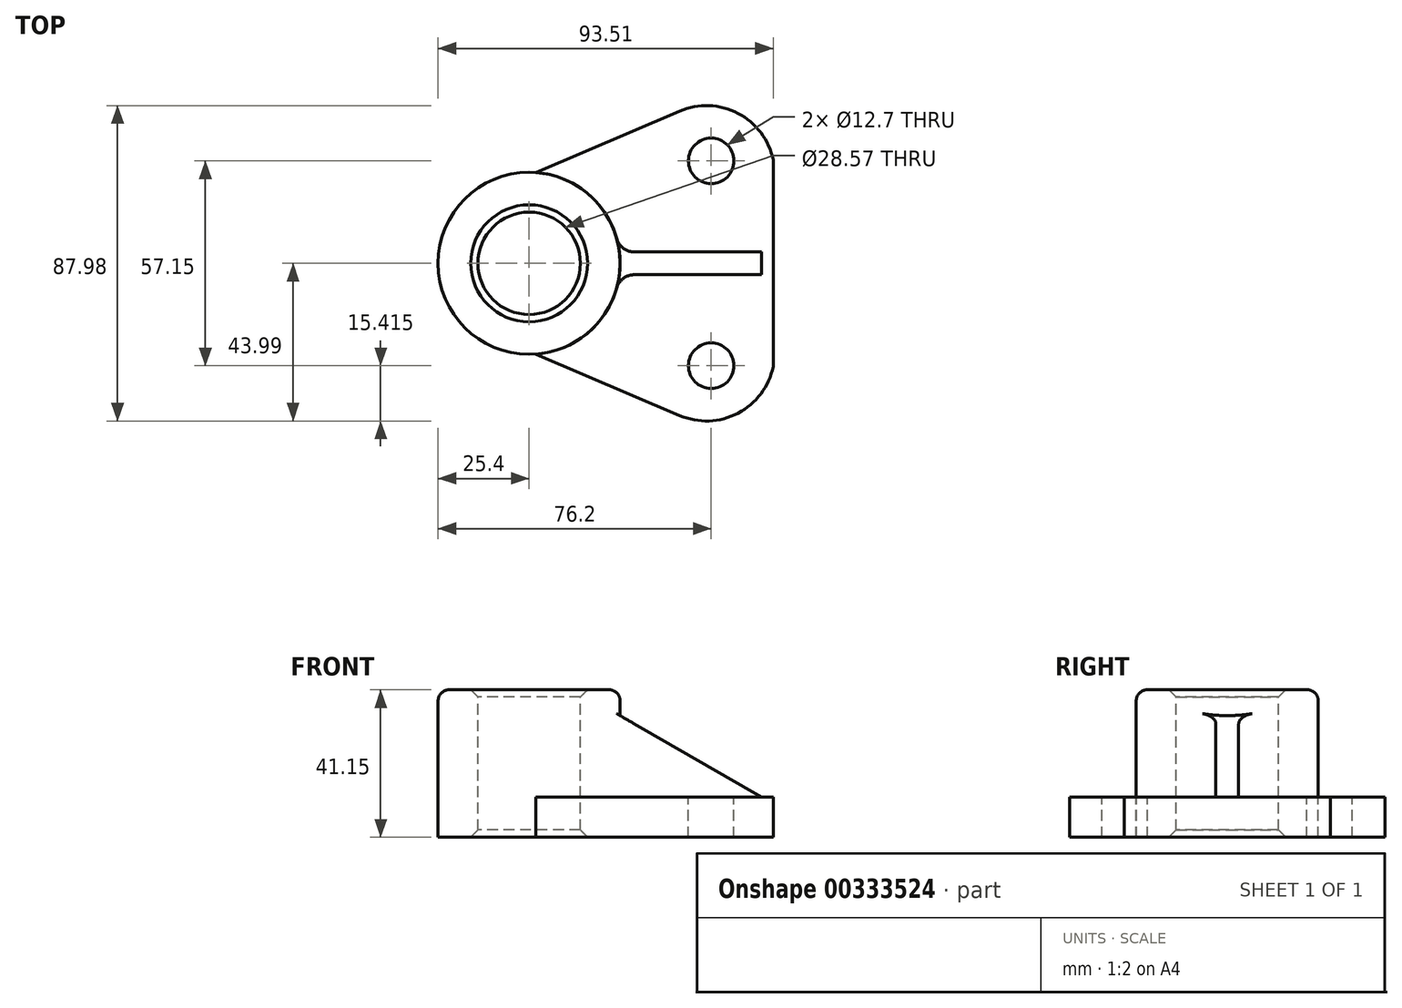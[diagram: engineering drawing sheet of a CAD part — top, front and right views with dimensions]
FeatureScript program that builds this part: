
annotation { "Feature Type Name" : "Feature", "Feature Type Description" : "" }
export const myFeature = defineFeature(function(context is Context, id is Id, definition is map)
    precondition{}
    {
        {
            var Q0;
            Q0=qCreatedBy(makeId("Top.planeOp"),FACE);
            var sketch = newSketch(context, id + "F0", { "sketchPlane" : qUnion([Q0])});
            skCircle(sketch, "E0", {"center": v(0, 0) * mm, "radius": 25.4 * mm});
            skCircle(sketch, "E1", {"center": v(50.8, -28.58) * mm, "radius": 6.35 * mm});
            skLineSegment(sketch, "E2", {"start": v(1.83, -25.33) * mm, "end": v(41.98, -42.47) * mm});
            skArc(sketch, "E3", {"start": v(41.98, -42.47) * mm, "mid": v(58.28, -41.83) * mm, "end": v(68.11, -28.8) * mm});
            skLineSegment(sketch, "E4.MirrorCS", {"start": v(1.83, 25.33) * mm, "end": v(41.98, 42.47) * mm});
            skArc(sketch, "E5.MirrorCS", {"start": v(41.98, 42.47) * mm, "mid": v(58.28, 41.83) * mm, "end": v(68.11, 28.8) * mm});
            skLineSegment(sketch, "E6", {"start": v(68.11, 28.8) * mm, "end": v(68.11, -28.8) * mm});
            skCircle(sketch, "E7.MirrorC", {"center": v(50.8, 28.58) * mm, "radius": 6.35 * mm});
            skCircle(sketch, "E8", {"center": v(0, 0) * mm, "radius": 14.29 * mm});
            skSolve(sketch);
        }
        {
            var Q0;
            Q0 = qSketchRegion(id + "F0", true);
            extrude(context, id + "F1", {"entities" : qUnion([Q0]), "oppositeDirection" : true, "depth" : 11.18 * mm, "offsetDistance" : 25.4 * mm});
        }
        {
            var Q0;
            Q0=qCreatedBy(makeId("Top.planeOp"),FACE);
            var sketch = newSketch(context, id + "F2", { "sketchPlane" : qUnion([Q0])});
            skCircle(sketch, "E9", {"center": v(0, 0) * mm, "radius": 25.4 * mm});
            skCircle(sketch, "E10", {"center": v(0, 0) * mm, "radius": 14.29 * mm});
            skSolve(sketch);
        }
        {
            var Q0;
            Q0 = qSketchRegion(id + "F2", true);
            extrude(context, id + "F3", {"entities" : qUnion([Q0]), "operationType" : NewBodyOperationType.ADD, "depth" : 29.97 * mm, "offsetDistance" : 25.4 * mm});
        }
        {
            var Q0;
            Q0=qCreatedBy(makeId("Front.planeOp"),FACE);
            var sketch = newSketch(context, id + "F4", { "sketchPlane" : qUnion([Q0])});
            skLineSegment(sketch, "E11", {"start": v(50.03, 8.53) * mm, "end": v(64.81, 0) * mm});
            skLineSegment(sketch, "E12", {"start": v(64.81, 0) * mm, "end": v(50.03, 0) * mm});
            skLineSegment(sketch, "E13", {"start": v(50.03, 8.53) * mm, "end": v(24.47, 23.29) * mm});
            skLineSegment(sketch, "E14", {"start": v(24.47, 23.29) * mm, "end": v(24.47, 0) * mm});
            skLineSegment(sketch, "E15", {"start": v(24.47, 0) * mm, "end": v(50.03, 0) * mm});
            skSolve(sketch);
        }
        {
            var Q0;
            Q0 = qSketchRegion(id + "F4", true);
            extrude(context, id + "F5", {"entities" : qUnion([Q0]), "operationType" : NewBodyOperationType.ADD, "depth" : 6.35 * mm, "offsetDistance" : 25.4 * mm, "symmetric" : true});
        }
        {
            var Q0;
            Q0=makeQuery(id+"F3.opExtrude","CAP_EDGE",EDGE,{"disambiguationData":[OSD([sQuery(id+"F2.wireOp",EDGE,"E9")])],"isStart":false});
            fillet(context, id + "F6", {"entities" : qUnion([Q0]), "radius" : 3.05 * mm, "tangentPropagation" : true, "allowEdgeOverflow" : false});
        }
        {
            var Q0;
            Q0=makeQuery(id+"F3.opExtrude","CAP_EDGE",EDGE,{"disambiguationData":[OSD([sQuery(id+"F2.wireOp",EDGE,"E10")])],"isStart":false});
            chamfer(context, id + "F7", {"entities" : qUnion([Q0]), "width" : 2.03 * mm, "tangentPropagation" : true});
        }
        {
            var Q0;
            Q0=makeQuery(id+"F1.opExtrude","CAP_EDGE",EDGE,{"disambiguationData":[OSD([sQuery(id+"F0.wireOp",EDGE,"E8")])],"isStart":false});
            chamfer(context, id + "F8", {"entities" : qUnion([Q0]), "width" : 2.03 * mm, "tangentPropagation" : true});
        }
        {
            var Q0;
            Q0=makeQuery(id+"F5.boolean.opBoolean","INTERSECT",EDGE,{"derivedFrom":[makeQuery(id+"F3.boolean.opBoolean","MERGE",FACE,{"derivedFrom":[makeQuery(id+"F1.opExtrude","SWEPT_FACE",FACE,{"disambiguationData":[OSD([sQuery(id+"F0.wireOp",EDGE,"E0")])]}),makeQuery(id+"F3.opExtrude","SWEPT_FACE",FACE,{"disambiguationData":[OSD([sQuery(id+"F2.wireOp",EDGE,"E9")])]})]}),makeQuery(id+"F5.opExtrude","CAP_FACE",FACE,{"disambiguationData":[OSD([sQuery(id+"F4.wireOp",EDGE,"E11"),sQuery(id+"F4.wireOp",EDGE,"E12"),sQuery(id+"F4.wireOp",EDGE,"E13"),sQuery(id+"F4.wireOp",EDGE,"E14"),sQuery(id+"F4.wireOp",EDGE,"E15")])],"isStart":false})]});
            var Q1;
            Q1=makeQuery(id+"F5.opExtrude","CAP_EDGE",EDGE,{"disambiguationData":[OSD([sQuery(id+"F4.wireOp",EDGE,"E12"),sQuery(id+"F4.wireOp",EDGE,"E15")])],"isStart":false});
            var Q2;
            {var subQ0=sQuery(id+"F2.wireOp",EDGE,"E9");var subQ1=sQuery(id+"F0.wireOp",EDGE,"E2");Q2=makeQuery(id+"F5.boolean.opBoolean","SPLIT",EDGE,{"disambiguationData":[TD([makeQuery(id+"F1.opExtrude","SWEPT_FACE",FACE,{"disambiguationData":[OSD([subQ1])]})])],"derivedFrom":makeQuery(id+"F3.opExtrude","CAP_EDGE",EDGE,{"disambiguationData":[OSD([subQ0])],"isStart":true})});}
            var Q3;
            Q3=makeQuery(id+"F5.boolean.opBoolean","INTERSECT",EDGE,{"derivedFrom":[makeQuery(id+"F3.boolean.opBoolean","MERGE",FACE,{"derivedFrom":[makeQuery(id+"F1.opExtrude","SWEPT_FACE",FACE,{"disambiguationData":[OSD([sQuery(id+"F0.wireOp",EDGE,"E0")])]}),makeQuery(id+"F3.opExtrude","SWEPT_FACE",FACE,{"disambiguationData":[OSD([sQuery(id+"F2.wireOp",EDGE,"E9")])]})]}),makeQuery(id+"F5.opExtrude","CAP_FACE",FACE,{"disambiguationData":[OSD([sQuery(id+"F4.wireOp",EDGE,"E11"),sQuery(id+"F4.wireOp",EDGE,"E12"),sQuery(id+"F4.wireOp",EDGE,"E13"),sQuery(id+"F4.wireOp",EDGE,"E14"),sQuery(id+"F4.wireOp",EDGE,"E15")])],"isStart":true})]});
            var Q4;
            {var subQ0=sQuery(id+"F2.wireOp",EDGE,"E9");var subQ1=sQuery(id+"F0.wireOp",EDGE,"E4.MirrorCS");Q4=makeQuery(id+"F5.boolean.opBoolean","SPLIT",EDGE,{"disambiguationData":[TD([makeQuery(id+"F1.opExtrude","SWEPT_FACE",FACE,{"disambiguationData":[OSD([subQ1])]})])],"derivedFrom":makeQuery(id+"F3.opExtrude","CAP_EDGE",EDGE,{"disambiguationData":[OSD([subQ0])],"isStart":true})});}
            var Q5;
            Q5=makeQuery(id+"F5.opExtrude","CAP_EDGE",EDGE,{"disambiguationData":[OSD([sQuery(id+"F4.wireOp",EDGE,"E12"),sQuery(id+"F4.wireOp",EDGE,"E15")])],"isStart":true});
            fillet(context, id + "F9", {"entities" : qUnion([Q0, Q1, Q2, Q3, Q4, Q5]), "radius" : 5.08 * mm, "tangentPropagation" : true, "allowEdgeOverflow" : false});
        }
    });
